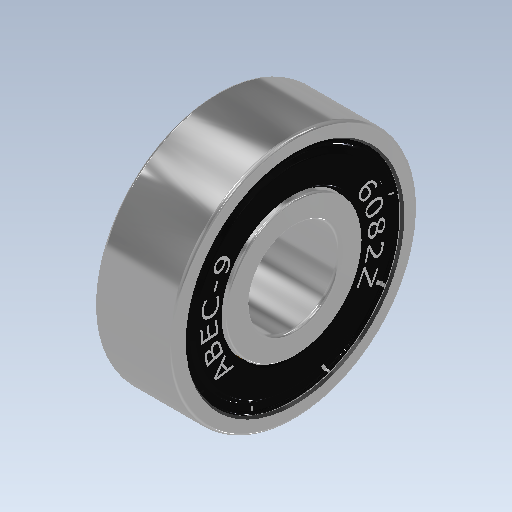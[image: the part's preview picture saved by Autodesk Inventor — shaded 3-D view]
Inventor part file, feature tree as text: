
AUTODESK INVENTOR PART (.ipt)
format: ipt  version: 2020.2 (Build 242310000, 310)  size: 2,061,824 bytes
history: native  units: mm
features: sketch x13, other x11, revolve x5, pattern_circular x4, extrude x4, mirror x2, projected_geometry x1
ambient origin geometry x8: Origin, YZ Plane, XZ Plane, XY Plane, X Axis, Y Axis, Z Axis, Center Point
bodies: Body1 (feature_tree), Body2 (feature_tree), Body3 (feature_tree), Body4 (feature_tree)
feature tree (40):
  other  "Sólido1"
  revolve  "Revolución1"  [1 undecoded]
  revolve  "Revolución2"  [1 undecoded]
  pattern_circular  "Patrón circular1"  [2 undecoded]
  revolve  "Revolución3"  [1 undecoded]
  extrude  "Extrusión1"  TaperAngle=90.0deg  [1 undecoded]
  pattern_circular  "Patrón circular2"  [2 undecoded]
  mirror  "Simetría1"
  other  "Repujado1"
  other  "Repujado2"
  extrude  "Extrusión2"  Depth=0.3mm
  sketch  "Boceto8"  dims[d30=0.3mm]
  revolve  "Revolución4"  Angle=90.0deg
  pattern_circular  "Patrón circular3"  Count=7 Angle=360.0deg
  sketch  "Boceto10"  dims[d33=0.6mm]
  mirror  "Simetría2"
  extrude  "Extrusión3"  Depth=0.3mm
  extrude  "Extrusión4"  Depth=0.3mm
  revolve  "Revolución5"  [1 undecoded]
  pattern_circular  "Patrón circular4"  [2 undecoded]
  sketch  "Boceto1"  dims[d0=22.0mm d1=8.0mm]
  other  "Imagen2"
  sketch  "Boceto2"  dims[d2=0.3mm d3=7.0mm]
  other  "Sólido2"
  sketch  "Boceto3"  dims[d4=7.0mm]
  other  "Sólido3"
  sketch  "Boceto4"  dims[d5=19.2mm]
  sketch  "Boceto5"  dims[d6=12.15mm]
  sketch  "Boceto6"  dims[d7=0.2mm]
  sketch  "Boceto7"  dims[d23=0.5mm]
  other  "Sólido4"
  projected_geometry  "Contorno proyectado1"
  sketch  "Boceto9"  dims[d31=0.2mm]
  sketch  "Boceto11"  dims[d35=12.217305mm]
  sketch  "Boceto12"  dims[d37=7.0mm]
  sketch  "Boceto13"  dims[d40=4.0mm d42=1.5125mm d43=3.025mm d44=90.0deg d45=3.99mm d46=2.0mm d47=90.0deg d48=70.0mm d49=360.0deg d69=0.3mm d72=0.1mm d76=0.05mm d80=0.15mm d83=0.056mm d84=0.052494mm d85=0.05mm d86=0.2mm d87=0.05mm d90=0.035mm d91=90.0deg d92=0.2mm d93=0.3mm d94=0.3mm d95=10.0mm d96=0.0mm d97=0.18mm d98=0.18mm d99=0.18mm d100=0.18mm d101=90.0mm d102=360.0deg d104=13.5mm d105=0.002mm d106=0.0mm d107=13.5mm d108=13.5mm d109=13.5mm d110=13.5mm d111=0.002mm d112=0.0mm d113=0.75mm d114=0.75mm d115=4.5mm d116=0.0mm d117=0.15mm d120=180.0deg d121=70.0mm d122=360.0deg d124=0.42mm d125=0.0mm d126=0.1mm d127=20.0mm d128=0.0mm d129=0.0mm d130=0.05mm d131=180.0deg d132=70.0mm d133=360.0deg]
  other  "Proyectar aristas de corte1"
  other  "Proyectar aristas de corte2"
  other  "Proyectar aristas de corte3"
  other  "Proyectar aristas de corte4"
note: 11 required parameter values undecoded (feature->parameter linkage not recoverable at this tier; creation-order binding heuristic only, values carry confidence <= 0.55)